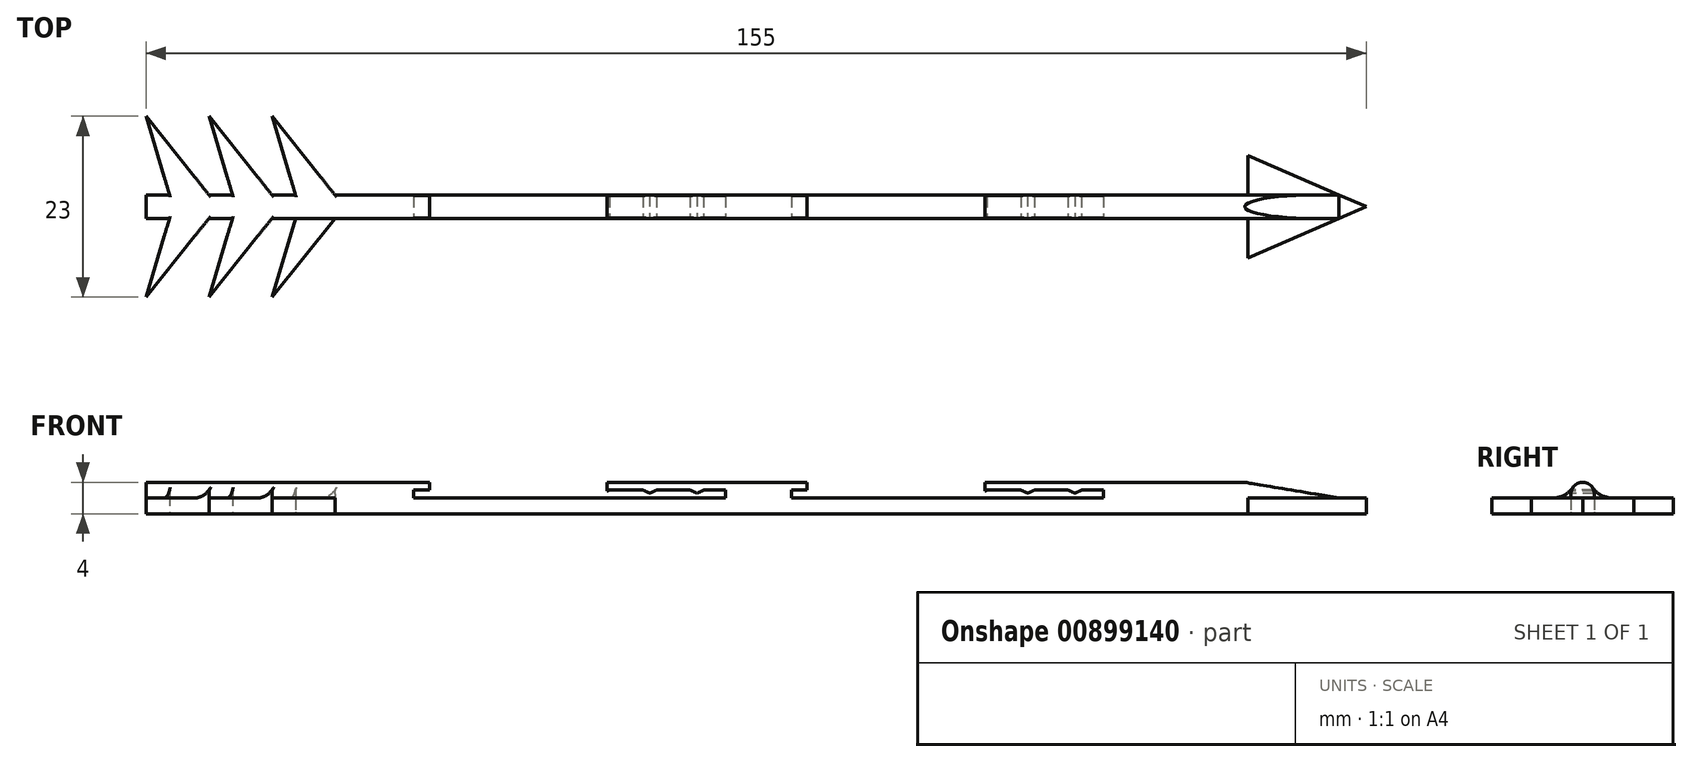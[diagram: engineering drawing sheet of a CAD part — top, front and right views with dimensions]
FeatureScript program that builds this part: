
annotation { "Feature Type Name" : "Feature", "Feature Type Description" : "" }
export const myFeature = defineFeature(function(context is Context, id is Id, definition is map)
    precondition{}
    {
        {
            var Q0;
            Q0=qCreatedBy(makeId("Top.planeOp"),FACE);
            var sketch = newSketch(context, id + "F0", { "sketchPlane" : qUnion([Q0])});
            skLineSegment(sketch, "E0.bottom", {"start": v(0, 0) * mm, "end": v(3, 0) * mm});
            skLineSegment(sketch, "E0.top", {"start": v(0, 3) * mm, "end": v(3, 3) * mm});
            skLineSegment(sketch, "E0.left", {"start": v(0, 0) * mm, "end": v(0, 3) * mm});
            skLineSegment(sketch, "E1", {"start": v(140, 0) * mm, "end": v(140, -5) * mm});
            skLineSegment(sketch, "E2", {"start": v(140, -5) * mm, "end": v(155, 1.5) * mm});
            skPoint(sketch, "E2.endSnap0", {"position": v(140, 1.5) * mm});
            skLineSegment(sketch, "E3", {"start": v(155, 1.5) * mm, "end": v(140, 8) * mm});
            skLineSegment(sketch, "E4", {"start": v(140, 8) * mm, "end": v(140, 3) * mm});
            skLineSegment(sketch, "E5", {"start": v(3, 3) * mm, "end": v(0, 13) * mm});
            skLineSegment(sketch, "E6", {"start": v(0, 13) * mm, "end": v(8, 3) * mm});
            skLineSegment(sketch, "E7", {"start": v(11, 3) * mm, "end": v(8, 13) * mm});
            skLineSegment(sketch, "E8", {"start": v(8, 13) * mm, "end": v(16, 3) * mm});
            skLineSegment(sketch, "E9", {"start": v(3, 0) * mm, "end": v(0, -10) * mm});
            skLineSegment(sketch, "E10", {"start": v(0, -10) * mm, "end": v(8, 0) * mm});
            skLineSegment(sketch, "E11", {"start": v(11, 0) * mm, "end": v(8, -10) * mm});
            skLineSegment(sketch, "E12", {"start": v(8, -10) * mm, "end": v(16, 0) * mm});
            skLineSegment(sketch, "E13", {"start": v(19, 0) * mm, "end": v(16, -10) * mm});
            skLineSegment(sketch, "E14", {"start": v(16, -10) * mm, "end": v(24, 0) * mm});
            skLineSegment(sketch, "E15", {"start": v(19, 3) * mm, "end": v(16, 13) * mm});
            skLineSegment(sketch, "E16", {"start": v(16, 13) * mm, "end": v(24, 3) * mm});
            skLineSegment(sketch, "E17.trimOffspring", {"start": v(8, 3) * mm, "end": v(11, 3) * mm});
            skLineSegment(sketch, "E18.trimOffspring", {"start": v(8, 0) * mm, "end": v(11, 0) * mm});
            skLineSegment(sketch, "E19.trimOffspring", {"start": v(16, 3) * mm, "end": v(19, 3) * mm});
            skLineSegment(sketch, "E20.trimOffspring", {"start": v(16, 0) * mm, "end": v(19, 0) * mm});
            skLineSegment(sketch, "E21.trimOffspring", {"start": v(24, 3) * mm, "end": v(140, 3) * mm});
            skLineSegment(sketch, "E22.trimOffspring", {"start": v(24, 0) * mm, "end": v(140, 0) * mm});
            skSolve(sketch);
        }
        {
            var Q0;
            Q0 = qSketchRegion(id + "F0", true);
            extrude(context, id + "F1", {"entities" : qUnion([Q0]), "depth" : 2 * mm, "offsetDistance" : 25 * mm});
        }
        {
            var Q0;
            Q0=makeQuery(id+"F1.opExtrude","SWEPT_FACE",FACE,{"disambiguationData":[OSD([sQuery(id+"F0.wireOp",EDGE,"E22.trimOffspring")])]});
            var sketch = newSketch(context, id + "F2", { "sketchPlane" : qUnion([Q0])});
            skLineSegment(sketch, "E23", {"start": v(0, 2) * mm, "end": v(34, 2) * mm});
            skLineSegment(sketch, "E24", {"start": v(155, 2) * mm, "end": v(155, 4) * mm});
            skLineSegment(sketch, "E25", {"start": v(155, 4) * mm, "end": v(0, 4) * mm});
            skLineSegment(sketch, "E26", {"start": v(0, 4) * mm, "end": v(0, 2) * mm});
            skLineSegment(sketch, "E27", {"start": v(34, 3) * mm, "end": v(34, 2) * mm});
            skLineSegment(sketch, "E28", {"start": v(52, 2.6) * mm, "end": v(52.86, 3) * mm});
            skLineSegment(sketch, "E29", {"start": v(57.14, 3) * mm, "end": v(58, 2.6) * mm});
            skLineSegment(sketch, "E30", {"start": v(58, 2.6) * mm, "end": v(58.86, 3) * mm});
            skLineSegment(sketch, "E31", {"start": v(63.14, 3) * mm, "end": v(64, 2.6) * mm});
            skLineSegment(sketch, "E32", {"start": v(64, 2.6) * mm, "end": v(64.86, 3) * mm});
            skLineSegment(sketch, "E33", {"start": v(69.14, 3) * mm, "end": v(70, 2.6) * mm});
            skLineSegment(sketch, "E34", {"start": v(70, 2.6) * mm, "end": v(70.86, 3) * mm});
            skLineSegment(sketch, "E35", {"start": v(73.6, 3) * mm, "end": v(73.6, 2) * mm});
            skLineSegment(sketch, "E36", {"start": v(82, 3) * mm, "end": v(82, 2) * mm});
            skLineSegment(sketch, "E37", {"start": v(100, 2.6) * mm, "end": v(100.86, 3) * mm});
            skLineSegment(sketch, "E38", {"start": v(105.14, 3) * mm, "end": v(106, 2.6) * mm});
            skLineSegment(sketch, "E39", {"start": v(106, 2.6) * mm, "end": v(106.86, 3) * mm});
            skLineSegment(sketch, "E40", {"start": v(111.14, 3) * mm, "end": v(112, 2.6) * mm});
            skLineSegment(sketch, "E41", {"start": v(112, 2.6) * mm, "end": v(112.86, 3) * mm});
            skLineSegment(sketch, "E42", {"start": v(117.14, 3) * mm, "end": v(118, 2.6) * mm});
            skLineSegment(sketch, "E43", {"start": v(118, 2.6) * mm, "end": v(118.86, 3) * mm});
            skLineSegment(sketch, "E44", {"start": v(121.6, 3) * mm, "end": v(121.6, 2) * mm});
            skLineSegment(sketch, "E45.trimOffspring", {"start": v(73.6, 2) * mm, "end": v(82, 2) * mm});
            skLineSegment(sketch, "E46.trimOffspring", {"start": v(121.6, 2) * mm, "end": v(155, 2) * mm});
            skLineSegment(sketch, "E47", {"start": v(52.86, 3) * mm, "end": v(57.14, 3) * mm});
            skLineSegment(sketch, "E48", {"start": v(58.86, 3) * mm, "end": v(63.14, 3) * mm});
            skLineSegment(sketch, "E49", {"start": v(64.86, 3) * mm, "end": v(69.14, 3) * mm});
            skLineSegment(sketch, "E50", {"start": v(70.86, 3) * mm, "end": v(73.6, 3) * mm});
            skPoint(sketch, "E51.orphan", {"position": v(55, 4) * mm});
            skPoint(sketch, "E52.orphan", {"position": v(61, 4) * mm});
            skPoint(sketch, "E53.orphan", {"position": v(67, 4) * mm});
            skPoint(sketch, "E54.orphan", {"position": v(73, 4) * mm});
            skPoint(sketch, "E55.orphan", {"position": v(73.6, 4) * mm});
            skLineSegment(sketch, "E56", {"start": v(103, 4) * mm, "end": v(103, 4) * mm});
            skPoint(sketch, "E57.orphan", {"position": v(103, 4) * mm});
            skLineSegment(sketch, "E58.trimOffspring", {"start": v(109, 4) * mm, "end": v(109, 4) * mm});
            skPoint(sketch, "E59.orphan", {"position": v(109, 4) * mm});
            skLineSegment(sketch, "E60.trimOffspring", {"start": v(115, 4) * mm, "end": v(115, 4) * mm});
            skPoint(sketch, "E61.orphan", {"position": v(115, 4) * mm});
            skLineSegment(sketch, "E62.trimOffspring", {"start": v(121, 4) * mm, "end": v(121.6, 4) * mm});
            skPoint(sketch, "E63.orphan", {"position": v(121, 4) * mm});
            skPoint(sketch, "E64.orphan", {"position": v(121.6, 4) * mm});
            skLineSegment(sketch, "E65", {"start": v(100.86, 3) * mm, "end": v(105.14, 3) * mm});
            skLineSegment(sketch, "E66", {"start": v(106.86, 3) * mm, "end": v(111.14, 3) * mm});
            skLineSegment(sketch, "E67", {"start": v(112.86, 3) * mm, "end": v(117.14, 3) * mm});
            skLineSegment(sketch, "E68", {"start": v(121.6, 3) * mm, "end": v(118.86, 3) * mm});
            skLineSegment(sketch, "E69", {"start": v(100, 2.6) * mm, "end": v(100, 4) * mm});
            skPoint(sketch, "E70.start.orphan", {"position": v(97, 4) * mm});
            skPoint(sketch, "E71.orphan", {"position": v(101.5, 3.3) * mm});
            skPoint(sketch, "E72.orphan", {"position": v(104.5, 3.3) * mm});
            skLineSegment(sketch, "E73", {"start": v(52, 2.6) * mm, "end": v(52, 4) * mm});
            skPoint(sketch, "E74.start.orphan", {"position": v(49, 4) * mm});
            skLineSegment(sketch, "E75", {"start": v(34, 4) * mm, "end": v(36, 4) * mm});
            skLineSegment(sketch, "E76", {"start": v(36, 4) * mm, "end": v(36, 3) * mm});
            skLineSegment(sketch, "E77", {"start": v(36, 3) * mm, "end": v(34, 3) * mm});
            skLineSegment(sketch, "E78", {"start": v(82, 4) * mm, "end": v(84, 4) * mm});
            skLineSegment(sketch, "E79", {"start": v(84, 4) * mm, "end": v(84, 3) * mm});
            skLineSegment(sketch, "E80", {"start": v(84, 3) * mm, "end": v(82, 3) * mm});
            skSolve(sketch);
        }
        {
            var Q0;
            Q0 = qSketchRegion(id + "F2", true);
            extrude(context, id + "F3", {"entities" : qUnion([Q0]), "operationType" : NewBodyOperationType.ADD, "oppositeDirection" : true, "depth" : 3 * mm, "offsetDistance" : 25 * mm});
        }
        {
            var Q0;
            {var subQ0=sQuery(id+"F2.wireOp",EDGE,"E25");Q0=makeQuery(id+"F3.opExtrude","CAP_EDGE",EDGE,{"disambiguationData":[OSD([subQ0]),TDD([makeQuery(id+"F2.imprint","IMPRINT",EDGE,{"disambiguationData":[TD([[makeQuery(id+"F2.imprint","INTERSECT",VERTEX,{"derivedFrom":[subQ0,sQuery(id+"F2.wireOp",EDGE,"E26")]}),1.0]])],"derivedFrom":subQ0})])],"isStart":true});}
            var Q1;
            {var subQ0=sQuery(id+"F2.wireOp",EDGE,"E25");Q1=makeQuery(id+"F3.opExtrude","CAP_EDGE",EDGE,{"disambiguationData":[OSD([subQ0]),TDD([makeQuery(id+"F2.imprint","IMPRINT",EDGE,{"disambiguationData":[TD([[makeQuery(id+"F2.imprint","INTERSECT",VERTEX,{"derivedFrom":[subQ0,sQuery(id+"F2.wireOp",EDGE,"E26")]}),1.0]])],"derivedFrom":subQ0})])],"isStart":false});}
            var Q2;
            {var subQ0=sQuery(id+"F2.wireOp",EDGE,"E25");Q2=makeQuery(id+"F3.opExtrude","CAP_EDGE",EDGE,{"disambiguationData":[OSD([subQ0]),TDD([makeQuery(id+"F2.imprint","IMPRINT",EDGE,{"disambiguationData":[TD([[makeQuery(id+"F2.imprint","INTERSECT",VERTEX,{"derivedFrom":[subQ0,sQuery(id+"F2.wireOp",EDGE,"E74")]}),1.0]])],"derivedFrom":subQ0})])],"isStart":true});}
            var Q3;
            {var subQ0=sQuery(id+"F2.wireOp",EDGE,"E25");Q3=makeQuery(id+"F3.opExtrude","CAP_EDGE",EDGE,{"disambiguationData":[OSD([subQ0]),TDD([makeQuery(id+"F2.imprint","IMPRINT",EDGE,{"disambiguationData":[TD([[makeQuery(id+"F2.imprint","INTERSECT",VERTEX,{"derivedFrom":[subQ0,sQuery(id+"F2.wireOp",EDGE,"E74")]}),1.0]])],"derivedFrom":subQ0})])],"isStart":false});}
            var Q4;
            {var subQ0=sQuery(id+"F2.wireOp",EDGE,"E25");Q4=makeQuery(id+"F3.opExtrude","CAP_EDGE",EDGE,{"disambiguationData":[OSD([subQ0]),TDD([makeQuery(id+"F2.imprint","IMPRINT",EDGE,{"disambiguationData":[TD([[makeQuery(id+"F2.imprint","INTERSECT",VERTEX,{"derivedFrom":[sQuery(id+"F2.wireOp",EDGE,"E24"),subQ0]}),-1.0]])],"derivedFrom":subQ0})])],"isStart":true});}
            var Q5;
            {var subQ0=sQuery(id+"F2.wireOp",EDGE,"E25");Q5=makeQuery(id+"F3.opExtrude","CAP_EDGE",EDGE,{"disambiguationData":[OSD([subQ0]),TDD([makeQuery(id+"F2.imprint","IMPRINT",EDGE,{"disambiguationData":[TD([[makeQuery(id+"F2.imprint","INTERSECT",VERTEX,{"derivedFrom":[sQuery(id+"F2.wireOp",EDGE,"E24"),subQ0]}),-1.0]])],"derivedFrom":subQ0})])],"isStart":false});}
            fillet(context, id + "F4", {"entities" : qUnion([Q0, Q1, Q2, Q3, Q4, Q5]), "radius" : 1.5 * mm, "tangentPropagation" : true, "allowEdgeOverflow" : false});
        }
        {
            var Q0;
            {var subQ1=sQuery(id+"F0.wireOp",EDGE,"E13");var subQ7=sQuery(id+"F2.wireOp",EDGE,"E23");Q0=makeQuery(id+"F3.boolean.opBoolean","SPLIT",EDGE,{"disambiguationData":[TD([makeQuery(id+"F1.opExtrude","SWEPT_FACE",FACE,{"disambiguationData":[OSD([subQ1])]})])],"derivedFrom":makeQuery(id+"F3.opExtrude","CAP_EDGE",EDGE,{"disambiguationData":[OSD([subQ7])],"isStart":true})});}
            var Q1;
            {var subQ5=sQuery(id+"F0.wireOp",EDGE,"E11");var subQ7=sQuery(id+"F2.wireOp",EDGE,"E23");Q1=makeQuery(id+"F3.boolean.opBoolean","SPLIT",EDGE,{"disambiguationData":[TD([makeQuery(id+"F1.opExtrude","SWEPT_FACE",FACE,{"disambiguationData":[OSD([subQ5])]})])],"derivedFrom":makeQuery(id+"F3.opExtrude","CAP_EDGE",EDGE,{"disambiguationData":[OSD([subQ7])],"isStart":true})});}
            var Q2;
            {var subQ1=sQuery(id+"F0.wireOp",EDGE,"E9");var subQ7=sQuery(id+"F2.wireOp",EDGE,"E23");Q2=makeQuery(id+"F3.boolean.opBoolean","SPLIT",EDGE,{"disambiguationData":[TD([makeQuery(id+"F1.opExtrude","SWEPT_FACE",FACE,{"disambiguationData":[OSD([subQ1])]})])],"derivedFrom":makeQuery(id+"F3.opExtrude","CAP_EDGE",EDGE,{"disambiguationData":[OSD([subQ7])],"isStart":true})});}
            var Q3;
            {var subQ3=sQuery(id+"F0.wireOp",EDGE,"E5");var subQ6=sQuery(id+"F2.wireOp",EDGE,"E23");Q3=makeQuery(id+"F3.boolean.opBoolean","SPLIT",EDGE,{"disambiguationData":[TD([makeQuery(id+"F1.opExtrude","SWEPT_FACE",FACE,{"disambiguationData":[OSD([subQ3])]})])],"derivedFrom":makeQuery(id+"F3.opExtrude","CAP_EDGE",EDGE,{"disambiguationData":[OSD([subQ6])],"isStart":false})});}
            var Q4;
            {var subQ0=sQuery(id+"F0.wireOp",EDGE,"E7");var subQ4=sQuery(id+"F2.wireOp",EDGE,"E23");Q4=makeQuery(id+"F3.boolean.opBoolean","SPLIT",EDGE,{"disambiguationData":[TD([makeQuery(id+"F1.opExtrude","SWEPT_FACE",FACE,{"disambiguationData":[OSD([subQ0])]})])],"derivedFrom":makeQuery(id+"F3.opExtrude","CAP_EDGE",EDGE,{"disambiguationData":[OSD([subQ4])],"isStart":false})});}
            var Q5;
            {var subQ1=sQuery(id+"F0.wireOp",EDGE,"E15");var subQ5=sQuery(id+"F2.wireOp",EDGE,"E23");Q5=makeQuery(id+"F3.boolean.opBoolean","SPLIT",EDGE,{"disambiguationData":[TD([makeQuery(id+"F1.opExtrude","SWEPT_FACE",FACE,{"disambiguationData":[OSD([subQ1])]})])],"derivedFrom":makeQuery(id+"F3.opExtrude","CAP_EDGE",EDGE,{"disambiguationData":[OSD([subQ5])],"isStart":false})});}
            fillet(context, id + "F5", {"entities" : qUnion([Q0, Q1, Q2, Q3, Q4, Q5]), "radius" : 3 * mm, "tangentPropagation" : true, "allowEdgeOverflow" : false});
        }
        {
            var Q0;
            {var subQ0=sQuery(id+"F2.wireOp",EDGE,"E25");Q0=makeQuery(id+"F5.opFillet","SPLIT",FACE,{"disambiguationData":[OD(0.0)],"derivedFrom":makeQuery(id+"F4.opFillet","SPLIT",FACE,{"disambiguationData":[OD(8.0)],"derivedFrom":makeQuery(id+"F3.boolean.opBoolean","MERGE",FACE,{"derivedFrom":[makeQuery(id+"F1.opExtrude","SWEPT_FACE",FACE,{"disambiguationData":[OSD([sQuery(id+"F0.wireOp",EDGE,"E0.bottom")])]}),makeQuery(id+"F1.opExtrude","SWEPT_FACE",FACE,{"disambiguationData":[OSD([sQuery(id+"F0.wireOp",EDGE,"E18.trimOffspring")])]}),makeQuery(id+"F1.opExtrude","SWEPT_FACE",FACE,{"disambiguationData":[OSD([sQuery(id+"F0.wireOp",EDGE,"E20.trimOffspring")])]}),makeQuery(id+"F1.opExtrude","SWEPT_FACE",FACE,{"disambiguationData":[OSD([sQuery(id+"F0.wireOp",EDGE,"E22.trimOffspring")])]}),makeQuery(id+"F3.opExtrude","CAP_FACE",FACE,{"disambiguationData":[OSD([sQuery(id+"F2.wireOp",EDGE,"E23"),subQ0,sQuery(id+"F2.wireOp",EDGE,"E26"),sQuery(id+"F2.wireOp",EDGE,"E27")])],"isStart":true}),makeQuery(id+"F3.opExtrude","CAP_FACE",FACE,{"disambiguationData":[OSD([sQuery(id+"F2.wireOp",EDGE,"E24"),subQ0,sQuery(id+"F2.wireOp",EDGE,"E70"),sQuery(id+"F2.wireOp",EDGE,"E37"),sQuery(id+"F2.wireOp",EDGE,"E38"),sQuery(id+"F2.wireOp",EDGE,"E39"),sQuery(id+"F2.wireOp",EDGE,"E40"),sQuery(id+"F2.wireOp",EDGE,"E41"),sQuery(id+"F2.wireOp",EDGE,"E42"),sQuery(id+"F2.wireOp",EDGE,"E43"),sQuery(id+"F2.wireOp",EDGE,"E44"),sQuery(id+"F2.wireOp",EDGE,"E46.trimOffspring"),sQuery(id+"F2.wireOp",EDGE,"E56"),sQuery(id+"F2.wireOp",EDGE,"E58.trimOffspring"),sQuery(id+"F2.wireOp",EDGE,"E60.trimOffspring"),sQuery(id+"F2.wireOp",EDGE,"E62.trimOffspring")])],"isStart":true}),makeQuery(id+"F3.opExtrude","CAP_FACE",FACE,{"disambiguationData":[OSD([subQ0,sQuery(id+"F2.wireOp",EDGE,"E74"),sQuery(id+"F2.wireOp",EDGE,"E28"),sQuery(id+"F2.wireOp",EDGE,"E29"),sQuery(id+"F2.wireOp",EDGE,"E30"),sQuery(id+"F2.wireOp",EDGE,"E31"),sQuery(id+"F2.wireOp",EDGE,"E32"),sQuery(id+"F2.wireOp",EDGE,"E33"),sQuery(id+"F2.wireOp",EDGE,"E34"),sQuery(id+"F2.wireOp",EDGE,"E35"),sQuery(id+"F2.wireOp",EDGE,"E36"),sQuery(id+"F2.wireOp",EDGE,"E45.trimOffspring"),sQuery(id+"F2.wireOp",EDGE,"E47"),sQuery(id+"F2.wireOp",EDGE,"E48"),sQuery(id+"F2.wireOp",EDGE,"E49"),sQuery(id+"F2.wireOp",EDGE,"E50")])],"isStart":true})]})})});}
            var sketch = newSketch(context, id + "F6", { "sketchPlane" : qUnion([Q0])});
            skLineSegment(sketch, "E81", {"start": v(151.54, 2) * mm, "end": v(127.46, 6) * mm});
            skLineSegment(sketch, "E82", {"start": v(127.46, 6) * mm, "end": v(155.08, 6) * mm});
            skLineSegment(sketch, "E83", {"start": v(155.08, 6) * mm, "end": v(155, 2) * mm});
            skLineSegment(sketch, "E84", {"start": v(155, 2) * mm, "end": v(151.54, 2) * mm});
            skSolve(sketch);
        }
        {
            var Q0;
            Q0 = qSketchRegion(id + "F6", true);
            extrude(context, id + "F7", {"entities" : qUnion([Q0]), "operationType" : NewBodyOperationType.REMOVE, "oppositeDirection" : true, "depth" : 25 * mm, "offsetDistance" : 25 * mm});
        }
        {
            var Q0;
            {var subQ0=sQuery(id+"F2.wireOp",EDGE,"E25");Q0=makeQuery(id+"F5.opFillet","SPLIT",FACE,{"disambiguationData":[OD(0.0)],"derivedFrom":makeQuery(id+"F3.boolean.opBoolean","MERGE",FACE,{"derivedFrom":[makeQuery(id+"F1.opExtrude","SWEPT_FACE",FACE,{"disambiguationData":[OSD([sQuery(id+"F0.wireOp",EDGE,"E0.bottom")])]}),makeQuery(id+"F1.opExtrude","SWEPT_FACE",FACE,{"disambiguationData":[OSD([sQuery(id+"F0.wireOp",EDGE,"E18.trimOffspring")])]}),makeQuery(id+"F1.opExtrude","SWEPT_FACE",FACE,{"disambiguationData":[OSD([sQuery(id+"F0.wireOp",EDGE,"E20.trimOffspring")])]}),makeQuery(id+"F1.opExtrude","SWEPT_FACE",FACE,{"disambiguationData":[OSD([sQuery(id+"F0.wireOp",EDGE,"E22.trimOffspring")])]}),makeQuery(id+"F3.opExtrude","CAP_FACE",FACE,{"disambiguationData":[OSD([sQuery(id+"F2.wireOp",EDGE,"E23"),subQ0,sQuery(id+"F2.wireOp",EDGE,"E26"),sQuery(id+"F2.wireOp",EDGE,"E27"),sQuery(id+"F2.wireOp",EDGE,"E75"),sQuery(id+"F2.wireOp",EDGE,"E76"),sQuery(id+"F2.wireOp",EDGE,"E77")])],"isStart":true}),makeQuery(id+"F3.opExtrude","CAP_FACE",FACE,{"disambiguationData":[OSD([sQuery(id+"F2.wireOp",EDGE,"E24"),subQ0,sQuery(id+"F2.wireOp",EDGE,"E37"),sQuery(id+"F2.wireOp",EDGE,"E38"),sQuery(id+"F2.wireOp",EDGE,"E39"),sQuery(id+"F2.wireOp",EDGE,"E40"),sQuery(id+"F2.wireOp",EDGE,"E41"),sQuery(id+"F2.wireOp",EDGE,"E42"),sQuery(id+"F2.wireOp",EDGE,"E43"),sQuery(id+"F2.wireOp",EDGE,"E44"),sQuery(id+"F2.wireOp",EDGE,"E46.trimOffspring"),sQuery(id+"F2.wireOp",EDGE,"E62.trimOffspring"),sQuery(id+"F2.wireOp",EDGE,"E65"),sQuery(id+"F2.wireOp",EDGE,"E66"),sQuery(id+"F2.wireOp",EDGE,"E67"),sQuery(id+"F2.wireOp",EDGE,"E68"),sQuery(id+"F2.wireOp",EDGE,"E69")])],"isStart":true}),makeQuery(id+"F3.opExtrude","CAP_FACE",FACE,{"disambiguationData":[OSD([subQ0,sQuery(id+"F2.wireOp",EDGE,"E28"),sQuery(id+"F2.wireOp",EDGE,"E29"),sQuery(id+"F2.wireOp",EDGE,"E30"),sQuery(id+"F2.wireOp",EDGE,"E31"),sQuery(id+"F2.wireOp",EDGE,"E32"),sQuery(id+"F2.wireOp",EDGE,"E33"),sQuery(id+"F2.wireOp",EDGE,"E34"),sQuery(id+"F2.wireOp",EDGE,"E35"),sQuery(id+"F2.wireOp",EDGE,"E36"),sQuery(id+"F2.wireOp",EDGE,"E45.trimOffspring"),sQuery(id+"F2.wireOp",EDGE,"E47"),sQuery(id+"F2.wireOp",EDGE,"E48"),sQuery(id+"F2.wireOp",EDGE,"E49"),sQuery(id+"F2.wireOp",EDGE,"E50"),sQuery(id+"F2.wireOp",EDGE,"E73"),sQuery(id+"F2.wireOp",EDGE,"E78"),sQuery(id+"F2.wireOp",EDGE,"E79"),sQuery(id+"F2.wireOp",EDGE,"E80")])],"isStart":true})]})});}
            var sketch = newSketch(context, id + "F8", { "sketchPlane" : qUnion([Q0])});
            skLineSegment(sketch, "E85.bottom", {"start": v(49.86, 2) * mm, "end": v(58.6, 2) * mm});
            skLineSegment(sketch, "E85.top", {"start": v(49.86, 5.91) * mm, "end": v(58.6, 5.91) * mm});
            skLineSegment(sketch, "E85.left", {"start": v(49.86, 2) * mm, "end": v(49.86, 5.91) * mm});
            skLineSegment(sketch, "E85.right", {"start": v(58.6, 2) * mm, "end": v(58.6, 5.91) * mm});
            skLineSegment(sketch, "E86.bottom", {"start": v(97.61, 2) * mm, "end": v(106.6, 2) * mm});
            skLineSegment(sketch, "E86.top", {"start": v(97.61, 5.33) * mm, "end": v(106.6, 5.33) * mm});
            skLineSegment(sketch, "E86.left", {"start": v(97.61, 2) * mm, "end": v(97.61, 5.33) * mm});
            skLineSegment(sketch, "E86.right", {"start": v(106.6, 2) * mm, "end": v(106.6, 5.33) * mm});
            skSolve(sketch);
        }
        {
            var Q0;
            Q0 = qSketchRegion(id + "F8", true);
            extrude(context, id + "F9", {"entities" : qUnion([Q0]), "operationType" : NewBodyOperationType.REMOVE, "oppositeDirection" : true, "depth" : 25 * mm, "offsetDistance" : 25 * mm});
        }
    });
